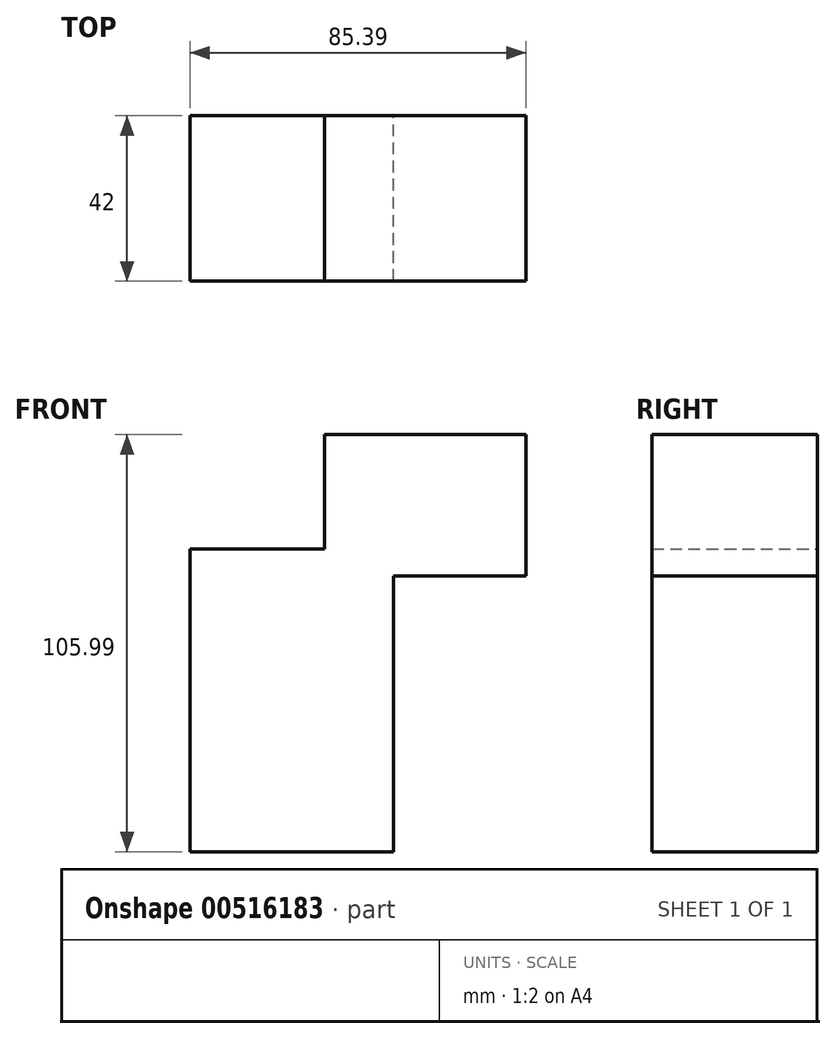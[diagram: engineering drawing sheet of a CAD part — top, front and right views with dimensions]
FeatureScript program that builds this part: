
annotation { "Feature Type Name" : "Feature", "Feature Type Description" : "" }
export const myFeature = defineFeature(function(context is Context, id is Id, definition is map)
    precondition{}
    {
        {
            var Q0;
            Q0=qCreatedBy(makeId("Front.planeOp"),FACE);
            var sketch = newSketch(context, id + "F0", { "sketchPlane" : qUnion([Q0])});
            skLineSegment(sketch, "E0.bottom", {"start": v(17.63, 0) * mm, "end": v(51.28, 0) * mm});
            skLineSegment(sketch, "E0.top", {"start": v(0, 35.94) * mm, "end": v(51.28, 35.94) * mm});
            skLineSegment(sketch, "E0.left", {"start": v(0, 6.87) * mm, "end": v(0, 35.94) * mm});
            skLineSegment(sketch, "E0.right", {"start": v(51.28, 0) * mm, "end": v(51.28, 35.94) * mm});
            skLineSegment(sketch, "E1.bottom", {"start": v(0, 6.87) * mm, "end": v(-34.1, 6.87) * mm});
            skLineSegment(sketch, "E1.top", {"start": v(17.63, -70.05) * mm, "end": v(-34.1, -70.05) * mm});
            skLineSegment(sketch, "E1.left", {"start": v(17.63, 6.87) * mm, "end": v(17.63, -70.05) * mm});
            skLineSegment(sketch, "E1.right", {"start": v(-34.1, 6.87) * mm, "end": v(-34.1, -70.05) * mm});
            skSolve(sketch);
        }
        {
            var Q0;
            {var subQ0=sQuery(id+"F0.wireOp",EDGE,"E0.bottom");Q0=makeQuery(id+"F0.imprint","IMPRINT",FACE,{"disambiguationData":[TD([[makeQuery(id+"F0.imprint","IMPRINT",EDGE,{"derivedFrom":subQ0}),1.0]])]});}
            extrude(context, id + "F1", {"entities" : qUnion([Q0]), "endBound" : BoundingType.SYMMETRIC, "depth" : 42 * mm, "offsetDistance" : 25 * mm});
        }
    });
